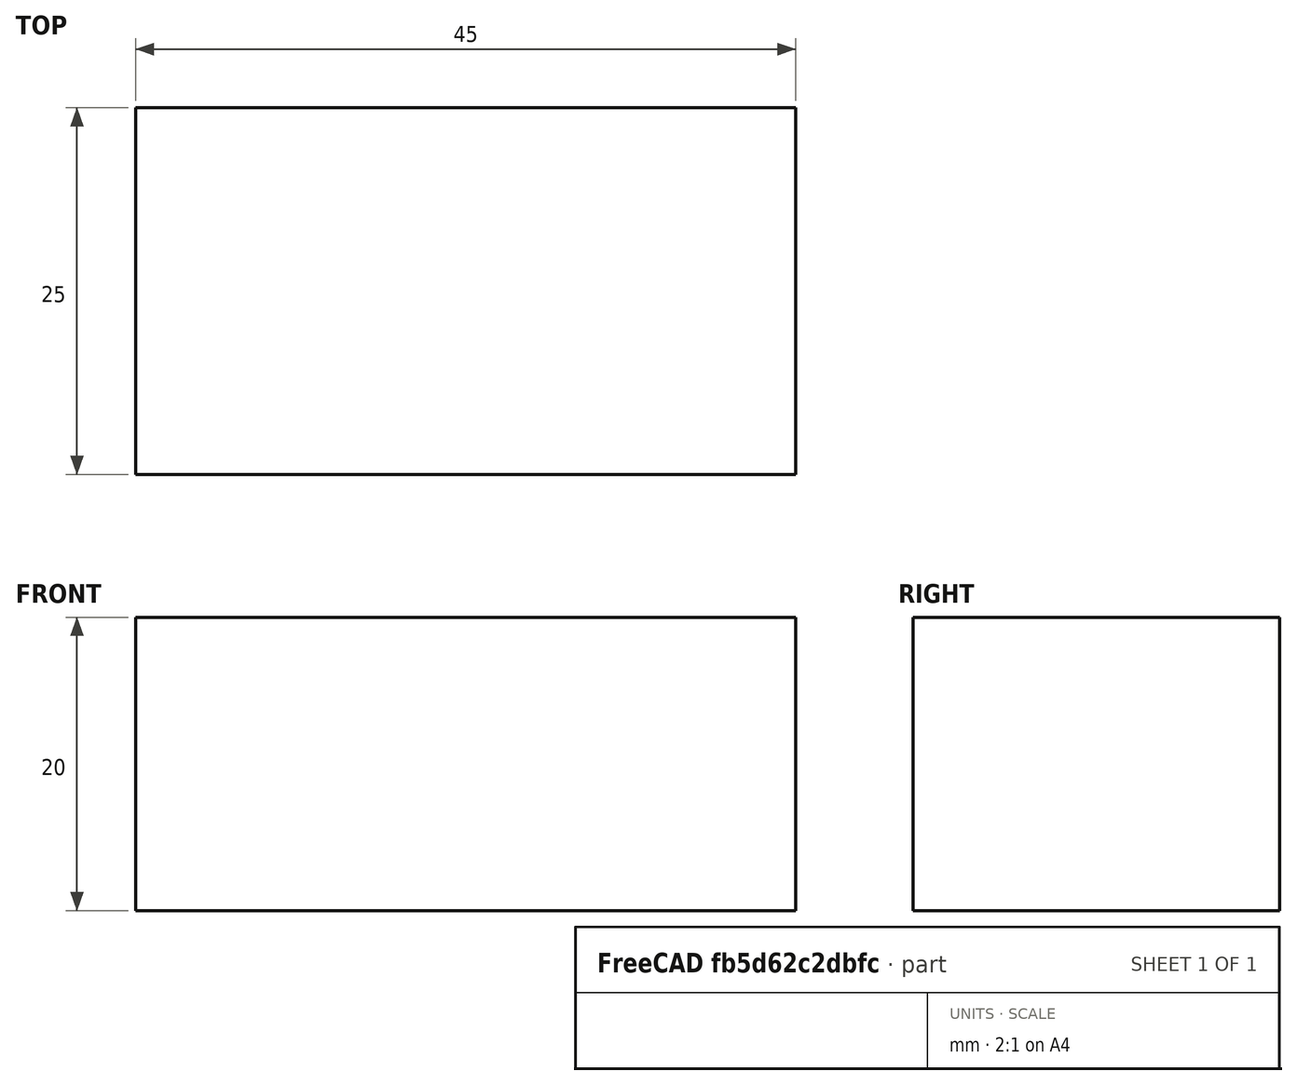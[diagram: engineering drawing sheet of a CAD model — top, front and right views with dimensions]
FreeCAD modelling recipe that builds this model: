
FCSTD DOCUMENT  (FreeCAD 0.21R33694 (Git))
Label: z_support
License: All rights reserved
LicenseURL: http://en.wikipedia.org/wiki/All_rights_reserved
objects: Sketcher::SketchObject×1, PartDesign::Pad×1, PartDesign::Body×1
note: 4 computed .brp shape members not serialized (recipe doc carries the construction recipe); baked Part::Feature solids carry a one-line shape summary decoded from their .brp

FEATURE [Sketcher::SketchObject] Sketch
  FullyConstrained = true
  MapMode = 5
  Support = -> [XY_Plane]
  sketch-geometry (4):
    g0: LineSegment StartX=0 StartY=0 StartZ=0 EndX=45 EndY=0 EndZ=0
    g1: LineSegment StartX=45 StartY=0 StartZ=0 EndX=45 EndY=25 EndZ=0
    g2: LineSegment StartX=45 StartY=25 StartZ=0 EndX=0 EndY=25 EndZ=0
    g3: LineSegment StartX=0 StartY=25 StartZ=0 EndX=0 EndY=0 EndZ=0
  constraints (11):
    c: Coincident(g0,g1)
    c: Coincident(g1,g2)
    c: Coincident(g2,g3)
    c: Coincident(g3,g0)
    c: Horizontal(g0)
    c: Horizontal(g2)
    c: Vertical(g1)
    c: Vertical(g3)
    c: Coincident(g0,g-1)
    c: DistanceY(g1,g1) = 25
    c: DistanceX(g2,g2) = 45
FEATURE [PartDesign::Pad] Pad
  Direction = (0,0,1)
  Length = 20
  Length2 = 10
  Profile = -> Sketch
  ReferenceAxis = -> Sketch [N_Axis]
  Type = 0
FEATURE [PartDesign::Body] Body
  Group = -> [Sketch,Pad]
  Origin = -> Origin
  Tip = -> Pad
